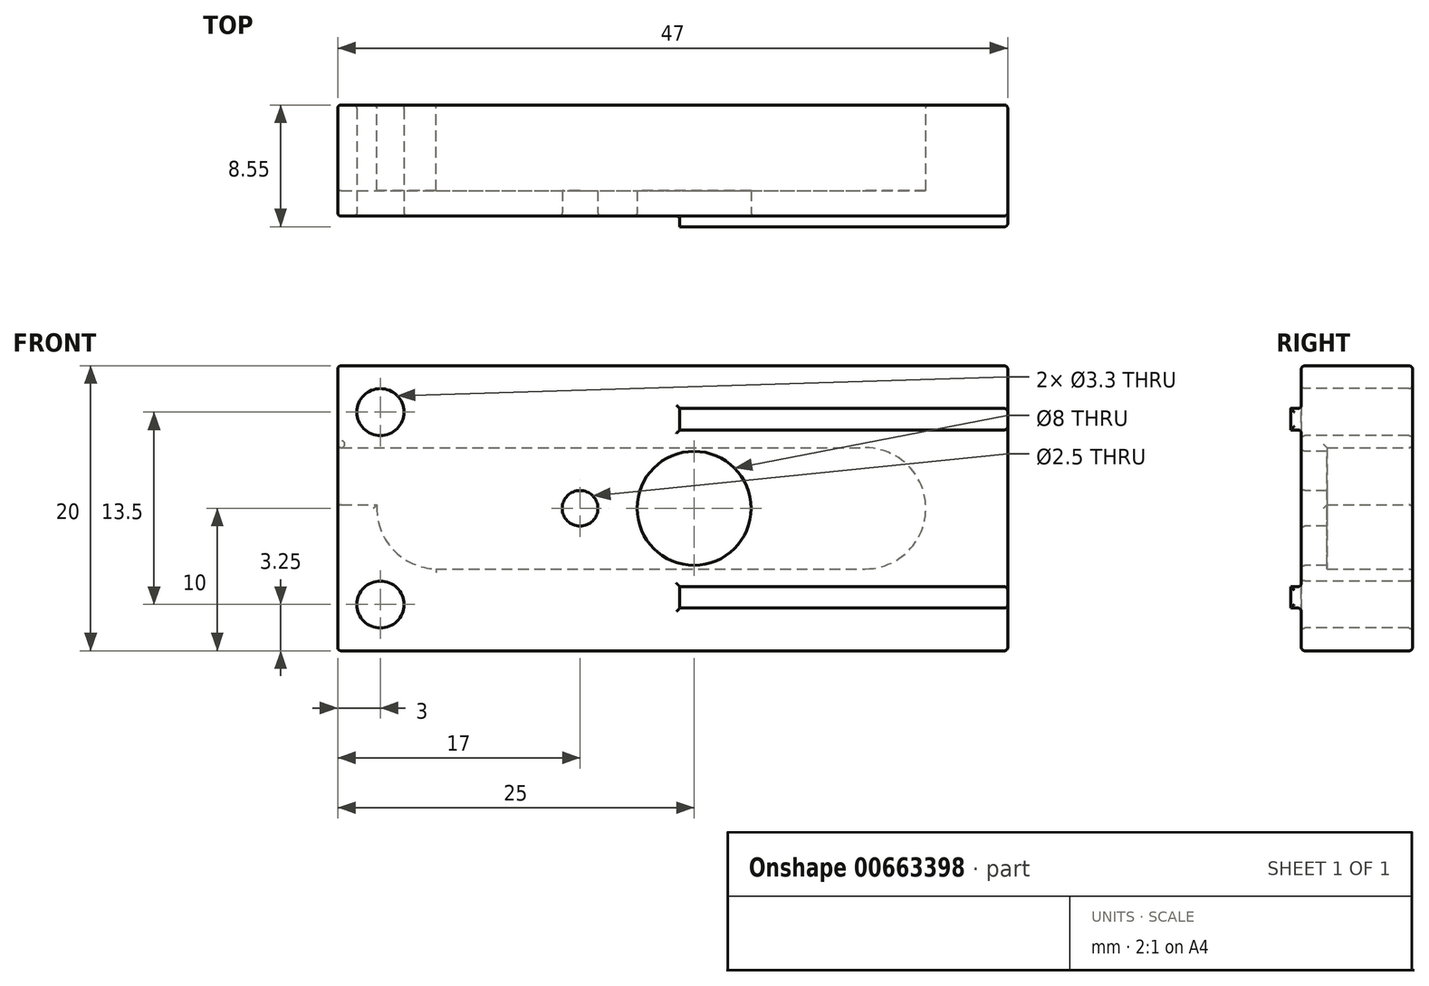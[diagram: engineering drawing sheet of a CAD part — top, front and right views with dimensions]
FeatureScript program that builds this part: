
annotation { "Feature Type Name" : "Feature", "Feature Type Description" : "" }
export const myFeature = defineFeature(function(context is Context, id is Id, definition is map)
    precondition{}
    {
        {
            var Q0;
            Q0=qCreatedBy(makeId("Front.planeOp"),FACE);
            var sketch = newSketch(context, id + "F0", { "sketchPlane" : qUnion([Q0])});
            skLineSegment(sketch, "E0.bottom", {"start": v(23.5, 10) * mm, "end": v(-23.5, 10) * mm});
            skLineSegment(sketch, "E0.top", {"start": v(23.5, -10) * mm, "end": v(-23.5, -10) * mm});
            skLineSegment(sketch, "E0.left", {"start": v(23.5, 10) * mm, "end": v(23.5, -10) * mm});
            skLineSegment(sketch, "E0.right", {"start": v(-23.5, 10) * mm, "end": v(-23.5, -10) * mm});
            skPoint(sketch, "E0.middle", {"position": v(0, 0) * mm});
            skSolve(sketch);
        }
        {
            var Q0;
            Q0=makeQuery(id+"F0.imprint","IMPRINT",FACE,{"disambiguationData":[TD([[makeQuery(id+"F0.imprint","IMPRINT",EDGE,{"derivedFrom":sQuery(id+"F0.wireOp",EDGE,"E0.bottom")}),1.0]])]});
            extrude(context, id + "F1", {"entities" : qUnion([Q0]), "depth" : 7.8 * mm, "offsetDistance" : 25 * mm});
        }
        {
            var Q0;
            Q0=makeQuery(id+"F1.opExtrude","CAP_FACE",FACE,{"disambiguationData":[OSD([sQuery(id+"F0.wireOp",EDGE,"E0.bottom"),sQuery(id+"F0.wireOp",EDGE,"E0.top"),sQuery(id+"F0.wireOp",EDGE,"E0.left"),sQuery(id+"F0.wireOp",EDGE,"E0.right")])],"isStart":false});
            var sketch = newSketch(context, id + "F2", { "sketchPlane" : qUnion([Q0])});
            skPoint(sketch, "E1", {"position": v(0.5, 10) * mm});
            skLineSegment(sketch, "E2", {"start": v(0.5, 10) * mm, "end": v(0.5, -10) * mm});
            skPoint(sketch, "E3", {"position": v(0.5, 5.5) * mm});
            skPoint(sketch, "E4", {"position": v(0.5, -5.5) * mm});
            skLineSegment(sketch, "E5", {"start": v(0.5, 5.5) * mm, "end": v(23.5, 5.5) * mm});
            skLineSegment(sketch, "E6", {"start": v(0.5, -5.5) * mm, "end": v(23.5, -5.5) * mm});
            skPoint(sketch, "E7", {"position": v(0.5, 7) * mm});
            skPoint(sketch, "E8", {"position": v(0.5, -7) * mm});
            skLineSegment(sketch, "E9", {"start": v(0.5, 7) * mm, "end": v(23.5, 7) * mm});
            skLineSegment(sketch, "E10", {"start": v(23.5, 7) * mm, "end": v(23.5, 5.5) * mm});
            skLineSegment(sketch, "E11", {"start": v(0.5, 7) * mm, "end": v(0.5, 5.5) * mm});
            skLineSegment(sketch, "E12", {"start": v(0.5, -7) * mm, "end": v(23.5, -7) * mm});
            skLineSegment(sketch, "E13", {"start": v(23.5, -5.5) * mm, "end": v(23.5, -7) * mm});
            skLineSegment(sketch, "E14", {"start": v(0.5, -5.5) * mm, "end": v(0.5, -7) * mm});
            skSolve(sketch);
        }
        {
            var Q0;
            Q0 = qSketchRegion(id + "F2", true);
            extrude(context, id + "F3", {"entities" : qUnion([Q0]), "operationType" : NewBodyOperationType.ADD, "depth" : .75 * mm, "offsetDistance" : 25 * mm});
        }
        {
            var Q0;
            Q0=makeQuery(id+"F1.opExtrude","CAP_FACE",FACE,{"disambiguationData":[OSD([sQuery(id+"F0.wireOp",EDGE,"E0.bottom"),sQuery(id+"F0.wireOp",EDGE,"E0.top"),sQuery(id+"F0.wireOp",EDGE,"E0.left"),sQuery(id+"F0.wireOp",EDGE,"E0.right")])],"isStart":false});
            var sketch = newSketch(context, id + "F4", { "sketchPlane" : qUnion([Q0])});
            skPoint(sketch, "E15", {"position": v(1.5, 0) * mm});
            skSolve(sketch);
        }
        {
            var Q0;
            Q0=sQuery(id+"F4.wireOp",VERTEX,"E15");
            var Q1;
            Q1=makeQuery(id+"F1.opExtrude","SWEPT_BODY",BODY,{"disambiguationData":[OSD([sQuery(id+"F0.wireOp",EDGE,"E0.bottom"),sQuery(id+"F0.wireOp",EDGE,"E0.top"),sQuery(id+"F0.wireOp",EDGE,"E0.left"),sQuery(id+"F0.wireOp",EDGE,"E0.right")])]});
            hole(context, id + "F5", {"style" : HoleStyle.SIMPLE, "endStyle" : HoleEndStyle.BLIND, "standardTappedOrClearance" : lookupTablePath({ "standard" : "ISO", "size" : "8", "type" : "Drilled" }), "standardBlindInLast" : lookupTablePath({ "standard" : "ISO", "size" : "8", "type" : "Drilled" }), "holeDiameter" : 8 * mm, "majorDiameter" : 5 * mm, "holeDepth" : 15 * mm, "isTappedThrough" : true, "tappedDepth" : 19 * mm, "tapClearance" : 3, "startFromSketch" : true, "locations" : qUnion([Q0]), "scope" : qUnion([Q1])});
        }
        {
            var Q0;
            Q0=makeQuery(id+"F1.opExtrude","CAP_FACE",FACE,{"disambiguationData":[OSD([sQuery(id+"F0.wireOp",EDGE,"E0.bottom"),sQuery(id+"F0.wireOp",EDGE,"E0.top"),sQuery(id+"F0.wireOp",EDGE,"E0.left"),sQuery(id+"F0.wireOp",EDGE,"E0.right")])],"isStart":false});
            var sketch = newSketch(context, id + "F6", { "sketchPlane" : qUnion([Q0])});
            skPoint(sketch, "E16", {"position": v(-20.5, -6.75) * mm});
            skPoint(sketch, "E17", {"position": v(-20.5, 6.75) * mm});
            skSolve(sketch);
        }
        {
            var Q0;
            Q0=sQuery(id+"F6.wireOp",VERTEX,"E16");
            var Q1;
            Q1=sQuery(id+"F6.wireOp",VERTEX,"E17");
            var Q2;
            Q2=makeQuery(id+"F1.opExtrude","SWEPT_BODY",BODY,{"disambiguationData":[OSD([sQuery(id+"F0.wireOp",EDGE,"E0.bottom"),sQuery(id+"F0.wireOp",EDGE,"E0.top"),sQuery(id+"F0.wireOp",EDGE,"E0.left"),sQuery(id+"F0.wireOp",EDGE,"E0.right")])]});
            hole(context, id + "F7", {"style" : HoleStyle.SIMPLE, "endStyle" : HoleEndStyle.BLIND, "standardTappedOrClearance" : lookupTablePath({ "standard" : "ISO", "fit" : "Normal", "size" : "M3", "type" : "Clearance" }), "standardBlindInLast" : lookupTablePath({ "fit" : "Standard", "standard" : "ISO", "size" : "M3", "type" : "Clearance" }), "holeDiameter" : 3.3 * mm, "majorDiameter" : 3 * mm, "holeDepth" : 20.5 * mm, "isTappedThrough" : true, "tappedDepth" : 19 * mm, "tapClearance" : 3, "startFromSketch" : true, "locations" : qUnion([Q0, Q1]), "scope" : qUnion([Q2])});
        }
        {
            var Q0;
            Q0=makeQuery(id+"F1.opExtrude","CAP_FACE",FACE,{"disambiguationData":[OSD([sQuery(id+"F0.wireOp",EDGE,"E0.bottom"),sQuery(id+"F0.wireOp",EDGE,"E0.top"),sQuery(id+"F0.wireOp",EDGE,"E0.left"),sQuery(id+"F0.wireOp",EDGE,"E0.right")])],"isStart":true});
            var sketch = newSketch(context, id + "F8", { "sketchPlane" : qUnion([Q0])});
            skPoint(sketch, "E18", {"position": v(16.5, 0) * mm});
            skPoint(sketch, "E19", {"position": v(-13.5, 0) * mm});
            skArc(sketch, "E20", {"start": v(16.4, -4.25) * mm, "mid": v(19.56, -2.95) * mm, "end": v(20.74, 0.25) * mm});
            skArc(sketch, "E21", {"start": v(-13.5, 4.25) * mm, "mid": v(-17.75, 0) * mm, "end": v(-13.5, -4.25) * mm});
            skLineSegment(sketch, "E22", {"start": v(16.6, -4.25) * mm, "end": v(-13.5, -4.25) * mm});
            skLineSegment(sketch, "E23", {"start": v(16.66, 4.25) * mm, "end": v(-13.5, 4.25) * mm});
            skLineSegment(sketch, "E24", {"start": v(16.66, 4.25) * mm, "end": v(23.5, 4.25) * mm});
            skLineSegment(sketch, "E25", {"start": v(23.5, 0.25) * mm, "end": v(23.5, 4.25) * mm});
            skLineSegment(sketch, "E26", {"start": v(23.5, 0.25) * mm, "end": v(20.74, 0.25) * mm});
            skArc(sketch, "E27.trimOffspring", {"start": v(16.66, 4.25) * mm, "mid": v(16.5, 4.25) * mm, "end": v(16.34, 4.25) * mm});
            skSolve(sketch);
        }
        {
            var Q0;
            {var subQ3=sQuery(id+"F8.wireOp",EDGE,"E21");Q0=makeQuery(id+"F8.imprint","IMPRINT",FACE,{"disambiguationData":[TD([[makeQuery(id+"F8.imprint","IMPRINT",EDGE,{"derivedFrom":subQ3}),1.0]])]});}
            extrude(context, id + "F9", {"entities" : qUnion([Q0]), "operationType" : NewBodyOperationType.REMOVE, "oppositeDirection" : true, "depth" : 6 * mm, "offsetDistance" : 25 * mm});
        }
        {
            var Q0;
            Q0=makeQuery(id+"F1.opExtrude","CAP_FACE",FACE,{"disambiguationData":[OSD([sQuery(id+"F0.wireOp",EDGE,"E0.bottom"),sQuery(id+"F0.wireOp",EDGE,"E0.top"),sQuery(id+"F0.wireOp",EDGE,"E0.left"),sQuery(id+"F0.wireOp",EDGE,"E0.right")])],"isStart":false});
            var sketch = newSketch(context, id + "F10", { "sketchPlane" : qUnion([Q0])});
            skPoint(sketch, "E28", {"position": v(-6.5, 0) * mm});
            skSolve(sketch);
        }
        {
            var Q0;
            Q0=sQuery(id+"F10.wireOp",VERTEX,"E28");
            var Q1;
            Q1=makeQuery(id+"F1.opExtrude","SWEPT_BODY",BODY,{"disambiguationData":[OSD([sQuery(id+"F0.wireOp",EDGE,"E0.bottom"),sQuery(id+"F0.wireOp",EDGE,"E0.top"),sQuery(id+"F0.wireOp",EDGE,"E0.left"),sQuery(id+"F0.wireOp",EDGE,"E0.right")])]});
            hole(context, id + "F11", {"style" : HoleStyle.SIMPLE, "endStyle" : HoleEndStyle.THROUGH, "standardTappedOrClearance" : lookupTablePath({ "standard" : "ISO", "engagement" : "75%", "pitch" : "0.5 mm", "size" : "M3", "type" : "Tapped" }), "standardBlindInLast" : lookupTablePath({ "standard" : "ISO", "engagement" : "75%", "pitch" : "0.5 mm", "size" : "M3", "type" : "Tapped" }), "holeDiameter" : 2.5 * mm, "majorDiameter" : 3 * mm, "showTappedDepth" : true, "isTappedThrough" : true, "tappedDepth" : 19 * mm, "tapClearance" : 3, "startFromSketch" : true, "locations" : qUnion([Q0]), "scope" : qUnion([Q1])});
        }
        {
            var Q0;
            Q0=makeQuery(id+"F1.opExtrude","CAP_FACE",FACE,{"disambiguationData":[OSD([sQuery(id+"F0.wireOp",EDGE,"E0.bottom"),sQuery(id+"F0.wireOp",EDGE,"E0.top"),sQuery(id+"F0.wireOp",EDGE,"E0.left"),sQuery(id+"F0.wireOp",EDGE,"E0.right")])],"isStart":false});
            var Q1;
            Q1=makeQuery(id+"F1.opExtrude","CAP_FACE",FACE,{"disambiguationData":[OSD([sQuery(id+"F0.wireOp",EDGE,"E0.bottom"),sQuery(id+"F0.wireOp",EDGE,"E0.top"),sQuery(id+"F0.wireOp",EDGE,"E0.left"),sQuery(id+"F0.wireOp",EDGE,"E0.right")])],"isStart":true});
            var Q2;
            Q2=makeQuery(id+"F1.opExtrude","SWEPT_FACE",FACE,{"disambiguationData":[OSD([sQuery(id+"F0.wireOp",EDGE,"E0.right")])]});
            var Q3;
            Q3=makeQuery(id+"F3.boolean.opBoolean","MERGE",FACE,{"derivedFrom":[makeQuery(id+"F1.opExtrude","SWEPT_FACE",FACE,{"disambiguationData":[OSD([sQuery(id+"F0.wireOp",EDGE,"E0.left")])]}),makeQuery(id+"F3.opExtrude","SWEPT_FACE",FACE,{"disambiguationData":[OSD([sQuery(id+"F2.wireOp",EDGE,"E10")])]}),makeQuery(id+"F3.opExtrude","SWEPT_FACE",FACE,{"disambiguationData":[OSD([sQuery(id+"F2.wireOp",EDGE,"E13")])]})]});
            fillet(context, id + "F12", {"entities" : qUnion([Q0, Q1, Q2, Q3]), "radius" : .25 * mm, "tangentPropagation" : true, "allowEdgeOverflow" : false});
        }
    });
